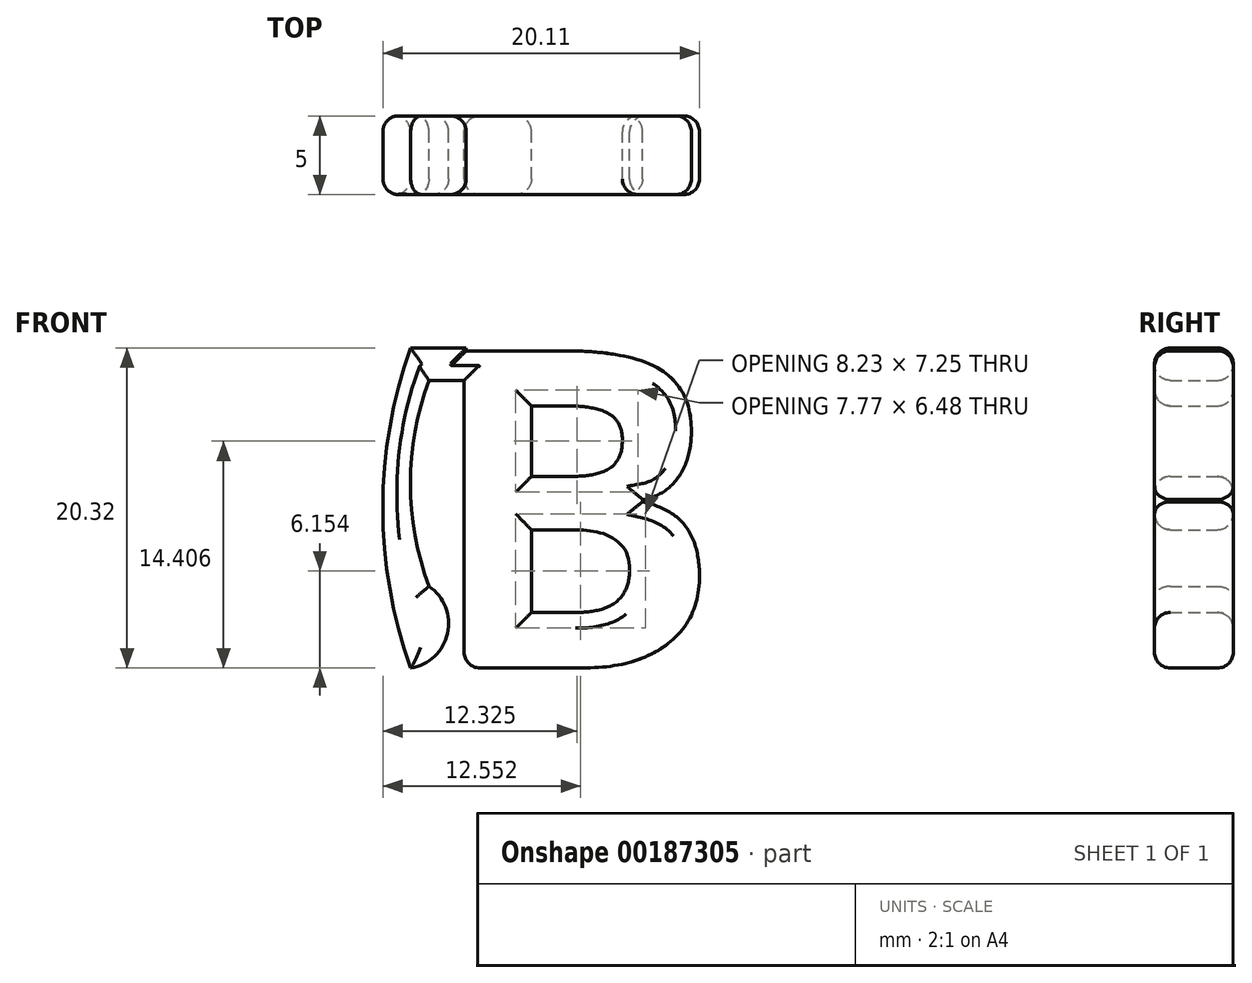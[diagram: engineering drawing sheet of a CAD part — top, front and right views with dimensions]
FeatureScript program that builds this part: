
annotation { "Feature Type Name" : "Feature", "Feature Type Description" : "" }
export const myFeature = defineFeature(function(context is Context, id is Id, definition is map)
    precondition{}
    {
        {
            var Q0;
            Q0=qCreatedBy(makeId("Front.planeOp"),FACE);
            var sketch = newSketch(context, id + "F0", { "sketchPlane" : qUnion([Q0])});
            skLineSegment(sketch, "E0", {"start": v(0, 20.32) * mm, "end": v(3.52, 20.32) * mm});
            skLineSegment(sketch, "E1", {"start": v(3.52, 20.32) * mm, "end": v(3.52, 18.27) * mm});
            skLineSegment(sketch, "E2", {"start": v(3.52, 18.27) * mm, "end": v(1.16, 18.27) * mm});
            skArc(sketch, "E3", {"start": v(0, 0) * mm, "mid": v(2.34, 2.2) * mm, "end": v(1.16, 5.18) * mm});
            skText(sketch, "E4", { "text": "B", "fontName": "OpenSans-Bold.ttf"});
            skArc(sketch, "E5", {"start": v(1.16, 18.27) * mm, "mid": v(-0.03, 11.72) * mm, "end": v(1.16, 5.18) * mm});
            skArc(sketch, "E6", {"start": v(0, 20.32) * mm, "mid": v(-1.77, 10.16) * mm, "end": v(0, 0) * mm});
            const initialGuessF0  = {"E4": [0.00086, 0, 1, 0, 0.02032]};
            skSetInitialGuess(sketch, initialGuessF0);
            skSolve(sketch);
        }
        {
            var Q0;
            Q0=qSketchRegion(id+"F0",true);
            extrude(context, id + "F1", {"entities" : qUnion([Q0]), "depth" : 5 * mm});
        }
        {
            var Q0;
            Q0=makeQuery(id+"F1.opExtrude","CAP_FACE",FACE,{"disambiguationData":[OSD([sQuery(id+"F0.wireOp",EDGE,"be7xAEPO-sKVT-0Ak3-rtqd-BYsUKJHZuXb5"),sQuery(id+"F0.wireOp",EDGE,"E0"),sQuery(id+"F0.wireOp",EDGE,"E1"),sQuery(id+"F0.wireOp",EDGE,"E2"),sQuery(id+"F0.wireOp",EDGE,"7xSTVDnR-abPq-wSY4-ofMi-LYckJfvl9Wuv"),sQuery(id+"F0.wireOp",EDGE,"E3"),sQuery(id+"F0.wireOp",EDGE,"E4.sketch_text.stroke-0"),sQuery(id+"F0.wireOp",EDGE,"E4.sketch_text.stroke-1"),sQuery(id+"F0.wireOp",EDGE,"E4.sketch_text.stroke-2"),sQuery(id+"F0.wireOp",EDGE,"E4.sketch_text.stroke-3"),sQuery(id+"F0.wireOp",EDGE,"E4.sketch_text.stroke-4"),sQuery(id+"F0.wireOp",EDGE,"E4.sketch_text.stroke-5"),sQuery(id+"F0.wireOp",EDGE,"E4.sketch_text.stroke-6"),sQuery(id+"F0.wireOp",EDGE,"E4.sketch_text.stroke-7"),sQuery(id+"F0.wireOp",EDGE,"E4.sketch_text.stroke-8"),sQuery(id+"F0.wireOp",EDGE,"E4.sketch_text.stroke-9")])],"isStart":false});
            var Q1;
            Q1=makeQuery(id+"F1.opExtrude","CAP_FACE",FACE,{"disambiguationData":[OSD([sQuery(id+"F0.wireOp",EDGE,"be7xAEPO-sKVT-0Ak3-rtqd-BYsUKJHZuXb5"),sQuery(id+"F0.wireOp",EDGE,"E0"),sQuery(id+"F0.wireOp",EDGE,"E1"),sQuery(id+"F0.wireOp",EDGE,"E2"),sQuery(id+"F0.wireOp",EDGE,"7xSTVDnR-abPq-wSY4-ofMi-LYckJfvl9Wuv"),sQuery(id+"F0.wireOp",EDGE,"E3"),sQuery(id+"F0.wireOp",EDGE,"E4.sketch_text.stroke-0"),sQuery(id+"F0.wireOp",EDGE,"E4.sketch_text.stroke-1"),sQuery(id+"F0.wireOp",EDGE,"E4.sketch_text.stroke-2"),sQuery(id+"F0.wireOp",EDGE,"E4.sketch_text.stroke-3"),sQuery(id+"F0.wireOp",EDGE,"E4.sketch_text.stroke-4"),sQuery(id+"F0.wireOp",EDGE,"E4.sketch_text.stroke-5"),sQuery(id+"F0.wireOp",EDGE,"E4.sketch_text.stroke-6"),sQuery(id+"F0.wireOp",EDGE,"E4.sketch_text.stroke-7"),sQuery(id+"F0.wireOp",EDGE,"E4.sketch_text.stroke-8"),sQuery(id+"F0.wireOp",EDGE,"E4.sketch_text.stroke-9")])],"isStart":true});
            fillet(context, id + "F2", {"entities" : qUnion([Q0, Q1]), "radius" : 1 * mm, "tangentPropagation" : true, "allowEdgeOverflow" : false});
        }
        {
            var Q0;
            Q0=makeQuery(id+"F1.opExtrude","SWEPT_EDGE",EDGE,{"disambiguationData":[OSD([sQuery(id+"F0.wireOp",EDGE,"E4.sketch_text.stroke-10"),sQuery(id+"F0.wireOp",EDGE,"E4.sketch_text.stroke-11")])]});
            fillet(context, id + "F3", {"entities" : qUnion([Q0]), "radius" : 1 * mm, "tangentPropagation" : true, "allowEdgeOverflow" : false});
        }
    });
